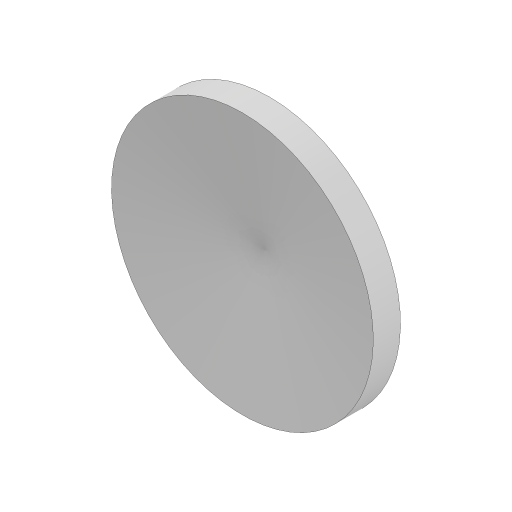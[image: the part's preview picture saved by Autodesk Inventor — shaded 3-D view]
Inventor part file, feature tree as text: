
AUTODESK INVENTOR PART (.ipt)
format: ipt  version: 2023.3 (Build 273359000, 359)  size: 109,568 bytes
history: native  units: mm
features: sketch x2, revolve x1
ambient origin geometry x8: Origin, YZ Plane, XZ Plane, XY Plane, X Axis, Y Axis, Z Axis, Center Point
bodies: Solid1 (feature_tree)
feature tree (3):
  sketch  "Sketch1"  dims[d0=6.4mm d1=3.2mm]
  revolve  "Revolution1"  [1 undecoded]
  sketch  "Sketch2"  dims[d3=0.1mm d4=1.745329mm d5=90.0deg]
note: 1 required parameter value undecoded (feature->parameter linkage not recoverable at this tier; creation-order binding heuristic only, values carry confidence <= 0.55)
